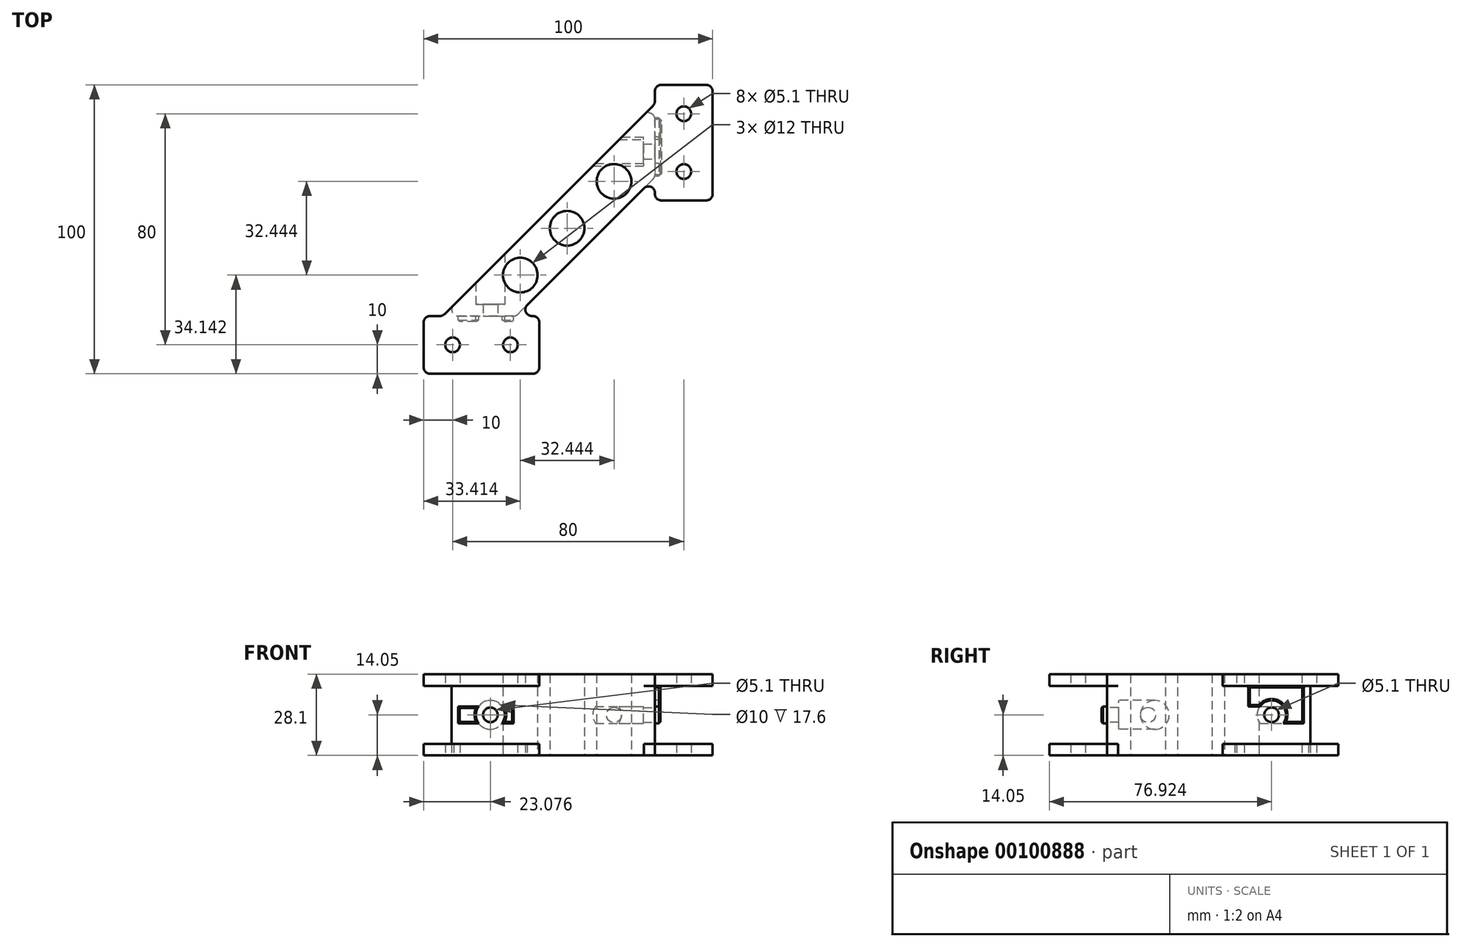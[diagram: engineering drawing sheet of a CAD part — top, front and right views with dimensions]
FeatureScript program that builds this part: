
annotation { "Feature Type Name" : "Feature", "Feature Type Description" : "" }
export const myFeature = defineFeature(function(context is Context, id is Id, definition is map)
    precondition{}
    {
        {
            var Q0;
            Q0=qCreatedBy(makeId("Top.planeOp"),FACE);
            var sketch = newSketch(context, id + "F0", { "sketchPlane" : qUnion([Q0])});
            skLineSegment(sketch, "E0.bottom", {"start": v(2.23, 0) * mm, "end": v(37.77, 0) * mm});
            skLineSegment(sketch, "E0.top", {"start": v(37.39, 20) * mm, "end": v(37.77, 20) * mm});
            skLineSegment(sketch, "E0.left", {"start": v(0, 2.23) * mm, "end": v(0, 17.77) * mm});
            skLineSegment(sketch, "E0.right", {"start": v(40, 2.23) * mm, "end": v(40, 17.77) * mm});
            skLineSegment(sketch, "E1", {"start": v(0, 0) * mm, "end": v(100, 0) * mm, "construction": true});
            skLineSegment(sketch, "E2", {"start": v(100, 0) * mm, "end": v(100, 100) * mm, "construction": true});
            skLineSegment(sketch, "E3.bottom", {"start": v(97.77, 100) * mm, "end": v(82.23, 100) * mm});
            skLineSegment(sketch, "E3.top", {"start": v(97.77, 60) * mm, "end": v(82.23, 60) * mm});
            skLineSegment(sketch, "E3.left", {"start": v(100, 97.77) * mm, "end": v(100, 62.23) * mm});
            skLineSegment(sketch, "E3.right", {"start": v(80, 62.61) * mm, "end": v(80, 62.23) * mm});
            skLineSegment(sketch, "E4", {"start": v(40, 20) * mm, "end": v(32, 20) * mm, "construction": true});
            skLineSegment(sketch, "E5", {"start": v(2.23, 20) * mm, "end": v(5.62, 20) * mm});
            skLineSegment(sketch, "E6", {"start": v(80, 60) * mm, "end": v(80, 68) * mm, "construction": true});
            skLineSegment(sketch, "E7", {"start": v(80, 97.77) * mm, "end": v(80, 94.38) * mm});
            skLineSegment(sketch, "E8", {"start": v(76.2, 64.2) * mm, "end": v(35.8, 23.8) * mm});
            skLineSegment(sketch, "E9", {"start": v(76.2, 89.65) * mm, "end": v(10.35, 23.8) * mm});
            skLineSegment(sketch, "E10", {"start": v(90, 80) * mm, "end": v(90, 70) * mm, "construction": true});
            skLineSegment(sketch, "E11", {"start": v(90, 80) * mm, "end": v(90, 90) * mm, "construction": true});
            skCircle(sketch, "E12", {"center": v(90, 90) * mm, "radius": 2.55 * mm});
            skCircle(sketch, "E13", {"center": v(90, 70) * mm, "radius": 2.55 * mm});
            skLineSegment(sketch, "E14", {"start": v(20, 10) * mm, "end": v(10, 10) * mm, "construction": true});
            skPoint(sketch, "E14.endSnap0", {"position": v(0, 10) * mm});
            skLineSegment(sketch, "E15", {"start": v(20, 10) * mm, "end": v(30, 10) * mm, "construction": true});
            skCircle(sketch, "E16", {"center": v(30, 10) * mm, "radius": 2.55 * mm});
            skCircle(sketch, "E17", {"center": v(10, 10) * mm, "radius": 2.55 * mm});
            skPoint(sketch, "E18.newPointA", {"position": v(32, 20) * mm});
            skArc(sketch, "E18.filletArc", {"start": v(35.8, 23.8) * mm, "mid": v(35.33, 21.38) * mm, "end": v(37.39, 20) * mm});
            skPoint(sketch, "E19.visualSharp", {"position": v(6.54, 20) * mm});
            skArc(sketch, "E19.filletArc", {"start": v(5.62, 20) * mm, "mid": v(6.47, 20.17) * mm, "end": v(7.2, 20.65) * mm});
            skArc(sketch, "E20.filletArc", {"start": v(80, 62.61) * mm, "mid": v(78.62, 64.67) * mm, "end": v(76.2, 64.2) * mm});
            skPoint(sketch, "E21.visualSharp", {"position": v(80, 93.46) * mm});
            skArc(sketch, "E21.filletArc", {"start": v(79.35, 92.8) * mm, "mid": v(79.83, 93.53) * mm, "end": v(80, 94.38) * mm});
            skLineSegment(sketch, "E22", {"start": v(80, 88.07) * mm, "end": v(80, 68.92) * mm});
            skLineSegment(sketch, "E23", {"start": v(11.93, 20) * mm, "end": v(31.08, 20) * mm});
            skCircle(sketch, "E24", {"center": v(33.41, 34.14) * mm, "radius": 6 * mm});
            skCircle(sketch, "E25", {"center": v(65.86, 66.59) * mm, "radius": 6 * mm});
            skCircle(sketch, "E26", {"center": v(49.64, 50.36) * mm, "radius": 6 * mm});
            skPoint(sketch, "E27.visualSharp", {"position": v(0, 20) * mm});
            skArc(sketch, "E27.filletArc", {"start": v(2.23, 20) * mm, "mid": v(0.65, 19.35) * mm, "end": v(0, 17.77) * mm});
            skPoint(sketch, "E28.visualSharp", {"position": v(0, 0) * mm});
            skArc(sketch, "E28.filletArc", {"start": v(0, 2.23) * mm, "mid": v(0.65, 0.65) * mm, "end": v(2.23, 0) * mm});
            skPoint(sketch, "E29.visualSharp", {"position": v(40, 0) * mm});
            skArc(sketch, "E29.filletArc", {"start": v(37.77, 0) * mm, "mid": v(39.35, 0.65) * mm, "end": v(40, 2.23) * mm});
            skPoint(sketch, "E30.visualSharp", {"position": v(40, 20) * mm});
            skArc(sketch, "E30.filletArc", {"start": v(40, 17.77) * mm, "mid": v(39.35, 19.35) * mm, "end": v(37.77, 20) * mm});
            skPoint(sketch, "E31.visualSharp", {"position": v(100, 60) * mm});
            skArc(sketch, "E31.filletArc", {"start": v(97.77, 60) * mm, "mid": v(99.35, 60.65) * mm, "end": v(100, 62.23) * mm});
            skPoint(sketch, "E32.visualSharp", {"position": v(80, 60) * mm});
            skArc(sketch, "E32.filletArc", {"start": v(80, 62.23) * mm, "mid": v(80.65, 60.65) * mm, "end": v(82.23, 60) * mm});
            skPoint(sketch, "E33.visualSharp", {"position": v(80, 100) * mm});
            skArc(sketch, "E33.filletArc", {"start": v(82.23, 100) * mm, "mid": v(80.65, 99.35) * mm, "end": v(80, 97.77) * mm});
            skPoint(sketch, "E34.visualSharp", {"position": v(100, 100) * mm});
            skArc(sketch, "E34.filletArc", {"start": v(100, 97.77) * mm, "mid": v(99.35, 99.35) * mm, "end": v(97.77, 100) * mm});
            skArc(sketch, "E35.filletArc", {"start": v(80, 88.07) * mm, "mid": v(78.62, 90.13) * mm, "end": v(76.2, 89.65) * mm});
            skLineSegment(sketch, "E36", {"start": v(79.35, 92.8) * mm, "end": v(76.2, 89.65) * mm});
            skLineSegment(sketch, "E37", {"start": v(76.2, 64.2) * mm, "end": v(79.35, 67.35) * mm});
            skArc(sketch, "E38.filletArc", {"start": v(79.35, 67.35) * mm, "mid": v(79.83, 68.07) * mm, "end": v(80, 68.92) * mm});
            skLineSegment(sketch, "E39", {"start": v(35.8, 23.8) * mm, "end": v(32.65, 20.65) * mm});
            skArc(sketch, "E40.filletArc", {"start": v(31.08, 20) * mm, "mid": v(31.93, 20.17) * mm, "end": v(32.65, 20.65) * mm});
            skArc(sketch, "E41.filletArc", {"start": v(10.35, 23.8) * mm, "mid": v(9.87, 21.38) * mm, "end": v(11.93, 20) * mm});
            skLineSegment(sketch, "E42", {"start": v(7.2, 20.65) * mm, "end": v(10.35, 23.8) * mm});
            skSolve(sketch);
        }
        {
            var Q0;
            Q0=makeQuery(id+"F0.imprint","IMPRINT",FACE,{"disambiguationData":[TD([[makeQuery(id+"F0.imprint","IMPRINT",EDGE,{"derivedFrom":sQuery(id+"F0.wireOp",EDGE,"E0.bottom")}),1.0]])]});
            var Q1;
            Q1=makeQuery(id+"F0.imprint","IMPRINT",FACE,{"disambiguationData":[TD([[makeQuery(id+"F0.imprint","IMPRINT",EDGE,{"derivedFrom":sQuery(id+"F0.wireOp",EDGE,"E3.bottom")}),1.0]])]});
            extrude(context, id + "F1", {"entities" : qUnion([Q0, Q1]), "depth" : 4 * mm});
        }
        {
            var Q0;
            Q0=makeQuery(id+"F0.imprint","IMPRINT",FACE,{"disambiguationData":[TD([[makeQuery(id+"F0.imprint","IMPRINT",EDGE,{"derivedFrom":sQuery(id+"F0.wireOp",EDGE,"E8")}),-1.0]])]});
            extrude(context, id + "F2", {"entities" : qUnion([Q0]), "depth" : 28.1 * mm});
        }
        {
            var Q0;
            Q0=makeQuery(id+"F0.imprint","IMPRINT",FACE,{"disambiguationData":[TD([[makeQuery(id+"F0.imprint","IMPRINT",EDGE,{"derivedFrom":sQuery(id+"F0.wireOp",EDGE,"E0.bottom")}),1.0]])]});
            var Q1;
            Q1=makeQuery(id+"F0.imprint","IMPRINT",FACE,{"disambiguationData":[TD([[makeQuery(id+"F0.imprint","IMPRINT",EDGE,{"derivedFrom":sQuery(id+"F0.wireOp",EDGE,"E3.bottom")}),1.0]])]});
            extrude(context, id + "F3", {"entities" : qUnion([Q0, Q1]), "operationType" : NewBodyOperationType.ADD, "depth" : 28.1 * mm, "hasSecondDirection" : true, "secondDirectionOppositeDirection" : false, "secondDirectionDepth" : 24 * mm});
        }
        {
            var Q0;
            Q0=makeQuery(id+"F2.opExtrude","SWEPT_FACE",FACE,{"disambiguationData":[OSD([sQuery(id+"F0.wireOp",EDGE,"E22")])]});
            var sketch = newSketch(context, id + "F4", { "sketchPlane" : qUnion([Q0])});
            skCircle(sketch, "E43", {"center": v(76.92, 14.05) * mm, "radius": 2.55 * mm});
            skCircle(sketch, "E44", {"center": v(76.92, 14.05) * mm, "radius": 5 * mm});
            skLineSegment(sketch, "E45", {"start": v(68.92, 11.15) * mm, "end": v(88.07, 11.15) * mm});
            skLineSegment(sketch, "E46", {"start": v(76.92, 16.95) * mm, "end": v(68.92, 16.95) * mm});
            skLineSegment(sketch, "E47", {"start": v(68.92, 16.95) * mm, "end": v(88.07, 16.95) * mm});
            skLineSegment(sketch, "E48", {"start": v(76.92, 14.05) * mm, "end": v(68.92, 14.05) * mm, "construction": true});
            skLineSegment(sketch, "E49", {"start": v(70.24, 14.05) * mm, "end": v(70.24, 16.95) * mm, "construction": true});
            skLineSegment(sketch, "E50", {"start": v(70.24, 14.05) * mm, "end": v(70.24, 11.15) * mm, "construction": true});
            skLineSegment(sketch, "E51.bottom", {"start": v(79.82, 11.15) * mm, "end": v(74.02, 11.15) * mm});
            skLineSegment(sketch, "E51.top", {"start": v(79.82, 16.95) * mm, "end": v(74.02, 16.95) * mm});
            skLineSegment(sketch, "E51.left", {"start": v(79.82, 11.15) * mm, "end": v(79.82, 16.95) * mm});
            skLineSegment(sketch, "E51.right", {"start": v(74.02, 11.15) * mm, "end": v(74.02, 16.95) * mm});
            skSolve(sketch);
        }
        {
            var Q0;
            Q0=makeQuery(id+"F4.imprint","IMPRINT",FACE,{"disambiguationData":[TD([[makeQuery(id+"F4.imprint","IMPRINT",EDGE,{"derivedFrom":sQuery(id+"F4.wireOp",EDGE,"E43")}),1.0]])]});
            extrude(context, id + "F5", {"entities" : qUnion([Q0]), "operationType" : NewBodyOperationType.REMOVE, "oppositeDirection" : true, "depth" : 25 * mm});
        }
        {
            var Q0;
            Q0=makeQuery(id+"F4.imprint","IMPRINT",FACE,{"disambiguationData":[TD([[makeQuery(id+"F4.imprint","IMPRINT",EDGE,{"derivedFrom":sQuery(id+"F4.wireOp",EDGE,"E43")}),-1.0]])]});
            var Q1;
            {var subQ0=sQuery(id+"F4.wireOp",EDGE,"E47");var subQ4=makeQuery(id+"F4.imprint","IMPRINT",VERTEX,{"derivedFrom":subQ0});Q1=makeQuery(id+"F4.imprint","IMPRINT",FACE,{"disambiguationData":[TD([[makeQuery(id+"F4.imprint","IMPRINT",EDGE,{"disambiguationData":[TD([[subQ4,1.0]])],"derivedFrom":subQ0}),1.0]])]});}
            var Q2;
            {var subQ0=sQuery(id+"F4.wireOp",EDGE,"E45");var subQ1=sQuery(id+"F4.wireOp",EDGE,"E44");var subQ2=makeQuery(id+"F4.imprint","INTERSECT",VERTEX,{"disambiguationData":[OD(0.0)],"derivedFrom":[subQ1,subQ0]});Q2=makeQuery(id+"F4.imprint","IMPRINT",FACE,{"disambiguationData":[TD([[makeQuery(id+"F4.imprint","IMPRINT",EDGE,{"disambiguationData":[TD([[subQ2,-1.0]])],"derivedFrom":subQ1}),1.0]])]});}
            var Q3;
            {var subQ5=sQuery(id+"F4.wireOp",EDGE,"E51.right");Q3=makeQuery(id+"F4.imprint","IMPRINT",FACE,{"disambiguationData":[TD([[makeQuery(id+"F4.imprint","IMPRINT",EDGE,{"derivedFrom":subQ5}),1.0]])]});}
            var Q4;
            {var subQ1=sQuery(id+"F4.wireOp",EDGE,"E47");var subQ4=sQuery(id+"F4.wireOp",EDGE,"E44");var subQ7=makeQuery(id+"F4.imprint","INTERSECT",VERTEX,{"disambiguationData":[OD(0.0)],"derivedFrom":[subQ4,subQ1]});Q4=makeQuery(id+"F4.imprint","IMPRINT",FACE,{"disambiguationData":[TD([[makeQuery(id+"F4.imprint","IMPRINT",EDGE,{"disambiguationData":[TD([[subQ7,1.0]])],"derivedFrom":subQ4}),1.0]])]});}
            var Q5;
            {var subQ5=sQuery(id+"F4.wireOp",EDGE,"E51.left");Q5=makeQuery(id+"F4.imprint","IMPRINT",FACE,{"disambiguationData":[TD([[makeQuery(id+"F4.imprint","IMPRINT",EDGE,{"derivedFrom":subQ5}),-1.0]])]});}
            extrude(context, id + "F6", {"entities" : qUnion([Q0, Q1, Q2, Q3, Q4, Q5]), "operationType" : NewBodyOperationType.REMOVE, "oppositeDirection" : true, "depth" : 51.78 * mm, "hasSecondDirection" : true, "secondDirectionOppositeDirection" : true, "secondDirectionDepth" : 4 * mm});
        }
        {
            var Q0;
            {var subQ0=sQuery(id+"F4.wireOp",EDGE,"E47");var subQ1=sQuery(id+"F4.wireOp",EDGE,"E44");var subQ2=makeQuery(id+"F4.imprint","INTERSECT",VERTEX,{"disambiguationData":[OD(0.0)],"derivedFrom":[subQ1,subQ0]});Q0=makeQuery(id+"F4.imprint","IMPRINT",FACE,{"disambiguationData":[TD([[makeQuery(id+"F4.imprint","IMPRINT",EDGE,{"disambiguationData":[TD([[subQ2,-1.0]])],"derivedFrom":subQ1}),-1.0]])]});}
            var Q1;
            {var subQ0=sQuery(id+"F4.wireOp",EDGE,"E47");var subQ1=sQuery(id+"F4.wireOp",EDGE,"E44");var subQ2=makeQuery(id+"F4.imprint","INTERSECT",VERTEX,{"disambiguationData":[OD(1.0)],"derivedFrom":[subQ1,subQ0]});Q1=makeQuery(id+"F4.imprint","IMPRINT",FACE,{"disambiguationData":[TD([[makeQuery(id+"F4.imprint","IMPRINT",EDGE,{"disambiguationData":[TD([[subQ2,1.0]])],"derivedFrom":subQ1}),-1.0]])]});}
            extrude(context, id + "F7", {"entities" : qUnion([Q0, Q1]), "operationType" : NewBodyOperationType.ADD, "depth" : 1.9 * mm});
        }
        {
            var Q0;
            Q0=makeQuery(id+"F2.opExtrude","SWEPT_FACE",FACE,{"disambiguationData":[OSD([sQuery(id+"F0.wireOp",EDGE,"E23")])]});
            var sketch = newSketch(context, id + "F8", { "sketchPlane" : qUnion([Q0])});
            skLineSegment(sketch, "E52", {"start": v(23.08, 14.05) * mm, "end": v(31.08, 14.05) * mm, "construction": true});
            skCircle(sketch, "E53", {"center": v(23.08, 14.05) * mm, "radius": 2.55 * mm});
            skCircle(sketch, "E54", {"center": v(23.08, 14.05) * mm, "radius": 5 * mm});
            skLineSegment(sketch, "E55", {"start": v(31.08, 16.95) * mm, "end": v(11.93, 16.95) * mm});
            skLineSegment(sketch, "E56", {"start": v(31.08, 11.15) * mm, "end": v(11.93, 11.15) * mm});
            skLineSegment(sketch, "E57", {"start": v(28.9, 14.05) * mm, "end": v(28.9, 16.95) * mm, "construction": true});
            skLineSegment(sketch, "E58", {"start": v(30.07, 14.05) * mm, "end": v(30.07, 11.15) * mm, "construction": true});
            skLineSegment(sketch, "E59.bottom", {"start": v(20.18, 11.15) * mm, "end": v(25.98, 11.15) * mm});
            skLineSegment(sketch, "E59.top", {"start": v(20.18, 16.95) * mm, "end": v(25.98, 16.95) * mm});
            skLineSegment(sketch, "E59.left", {"start": v(20.18, 11.15) * mm, "end": v(20.18, 16.95) * mm});
            skLineSegment(sketch, "E59.right", {"start": v(25.98, 11.15) * mm, "end": v(25.98, 16.95) * mm});
            skSolve(sketch);
        }
        {
            var Q0;
            Q0=makeQuery(id+"F8.imprint","IMPRINT",FACE,{"disambiguationData":[TD([[makeQuery(id+"F8.imprint","IMPRINT",EDGE,{"derivedFrom":sQuery(id+"F8.wireOp",EDGE,"E53")}),1.0]])]});
            extrude(context, id + "F9", {"entities" : qUnion([Q0]), "operationType" : NewBodyOperationType.REMOVE, "oppositeDirection" : true, "depth" : 22.92 * mm});
        }
        {
            var Q0;
            Q0=makeQuery(id+"F8.imprint","IMPRINT",FACE,{"disambiguationData":[TD([[makeQuery(id+"F8.imprint","IMPRINT",EDGE,{"derivedFrom":sQuery(id+"F8.wireOp",EDGE,"E53")}),-1.0]])]});
            var Q1;
            {var subQ0=sQuery(id+"F8.wireOp",EDGE,"E55");var subQ1=sQuery(id+"F8.wireOp",EDGE,"E54");var subQ2=makeQuery(id+"F8.imprint","INTERSECT",VERTEX,{"disambiguationData":[OD(0.0)],"derivedFrom":[subQ1,subQ0]});Q1=makeQuery(id+"F8.imprint","IMPRINT",FACE,{"disambiguationData":[TD([[makeQuery(id+"F8.imprint","IMPRINT",EDGE,{"disambiguationData":[TD([[subQ2,1.0]])],"derivedFrom":subQ1}),1.0]])]});}
            var Q2;
            {var subQ0=sQuery(id+"F8.wireOp",EDGE,"E56");var subQ1=sQuery(id+"F8.wireOp",EDGE,"E54");var subQ2=makeQuery(id+"F8.imprint","INTERSECT",VERTEX,{"disambiguationData":[OD(0.0)],"derivedFrom":[subQ1,subQ0]});Q2=makeQuery(id+"F8.imprint","IMPRINT",FACE,{"disambiguationData":[TD([[makeQuery(id+"F8.imprint","IMPRINT",EDGE,{"disambiguationData":[TD([[subQ2,-1.0]])],"derivedFrom":subQ1}),1.0]])]});}
            var Q3;
            {var subQ5=sQuery(id+"F8.wireOp",EDGE,"E59.left");Q3=makeQuery(id+"F8.imprint","IMPRINT",FACE,{"disambiguationData":[TD([[makeQuery(id+"F8.imprint","IMPRINT",EDGE,{"derivedFrom":subQ5}),1.0]])]});}
            var Q4;
            {var subQ5=sQuery(id+"F8.wireOp",EDGE,"E59.right");Q4=makeQuery(id+"F8.imprint","IMPRINT",FACE,{"disambiguationData":[TD([[makeQuery(id+"F8.imprint","IMPRINT",EDGE,{"derivedFrom":subQ5}),-1.0]])]});}
            extrude(context, id + "F10", {"entities" : qUnion([Q0, Q1, Q2, Q3, Q4]), "operationType" : NewBodyOperationType.REMOVE, "oppositeDirection" : true, "depth" : 25 * mm, "hasSecondDirection" : true, "secondDirectionOppositeDirection" : true, "secondDirectionDepth" : 4 * mm});
        }
        {
            var Q0;
            {var subQ0=sQuery(id+"F8.wireOp",EDGE,"E55");var subQ1=sQuery(id+"F8.wireOp",EDGE,"E54");var subQ2=makeQuery(id+"F8.imprint","INTERSECT",VERTEX,{"disambiguationData":[OD(0.0)],"derivedFrom":[subQ1,subQ0]});Q0=makeQuery(id+"F8.imprint","IMPRINT",FACE,{"disambiguationData":[TD([[makeQuery(id+"F8.imprint","IMPRINT",EDGE,{"disambiguationData":[TD([[subQ2,-1.0]])],"derivedFrom":subQ1}),-1.0]])]});}
            var Q1;
            {var subQ0=sQuery(id+"F8.wireOp",EDGE,"E55");var subQ1=sQuery(id+"F8.wireOp",EDGE,"E54");var subQ2=makeQuery(id+"F8.imprint","INTERSECT",VERTEX,{"disambiguationData":[OD(1.0)],"derivedFrom":[subQ1,subQ0]});Q1=makeQuery(id+"F8.imprint","IMPRINT",FACE,{"disambiguationData":[TD([[makeQuery(id+"F8.imprint","IMPRINT",EDGE,{"disambiguationData":[TD([[subQ2,1.0]])],"derivedFrom":subQ1}),-1.0]])]});}
            extrude(context, id + "F11", {"entities" : qUnion([Q0, Q1]), "operationType" : NewBodyOperationType.ADD, "depth" : 1.9 * mm});
        }
        {
            var Q0;
            Q0=makeQuery(id+"F11.opExtrude","CAP_FACE",FACE,{"disambiguationData":[OSD([sQuery(id+"F0.wireOp",EDGE,"E23"),sQuery(id+"F0.wireOp",EDGE,"E40.filletArc"),sQuery(id+"F0.wireOp",EDGE,"E41.filletArc"),sQuery(id+"F8.wireOp",EDGE,"E53"),sQuery(id+"F8.wireOp",EDGE,"E55"),sQuery(id+"F8.wireOp",EDGE,"E56")])],"isStart":false});
            var Q1;
            Q1=makeQuery(id+"F7.opExtrude","CAP_FACE",FACE,{"disambiguationData":[OSD([sQuery(id+"F0.wireOp",EDGE,"E22"),sQuery(id+"F0.wireOp",EDGE,"E35.filletArc"),sQuery(id+"F0.wireOp",EDGE,"E38.filletArc"),sQuery(id+"F4.wireOp",EDGE,"E43"),sQuery(id+"F4.wireOp",EDGE,"E45"),sQuery(id+"F4.wireOp",EDGE,"E47")])],"isStart":false});
            chamfer(context, id + "F12", {"entities" : qUnion([Q0, Q1]), "width" : .5 * mm, "tangentPropagation" : true});
        }
    });
